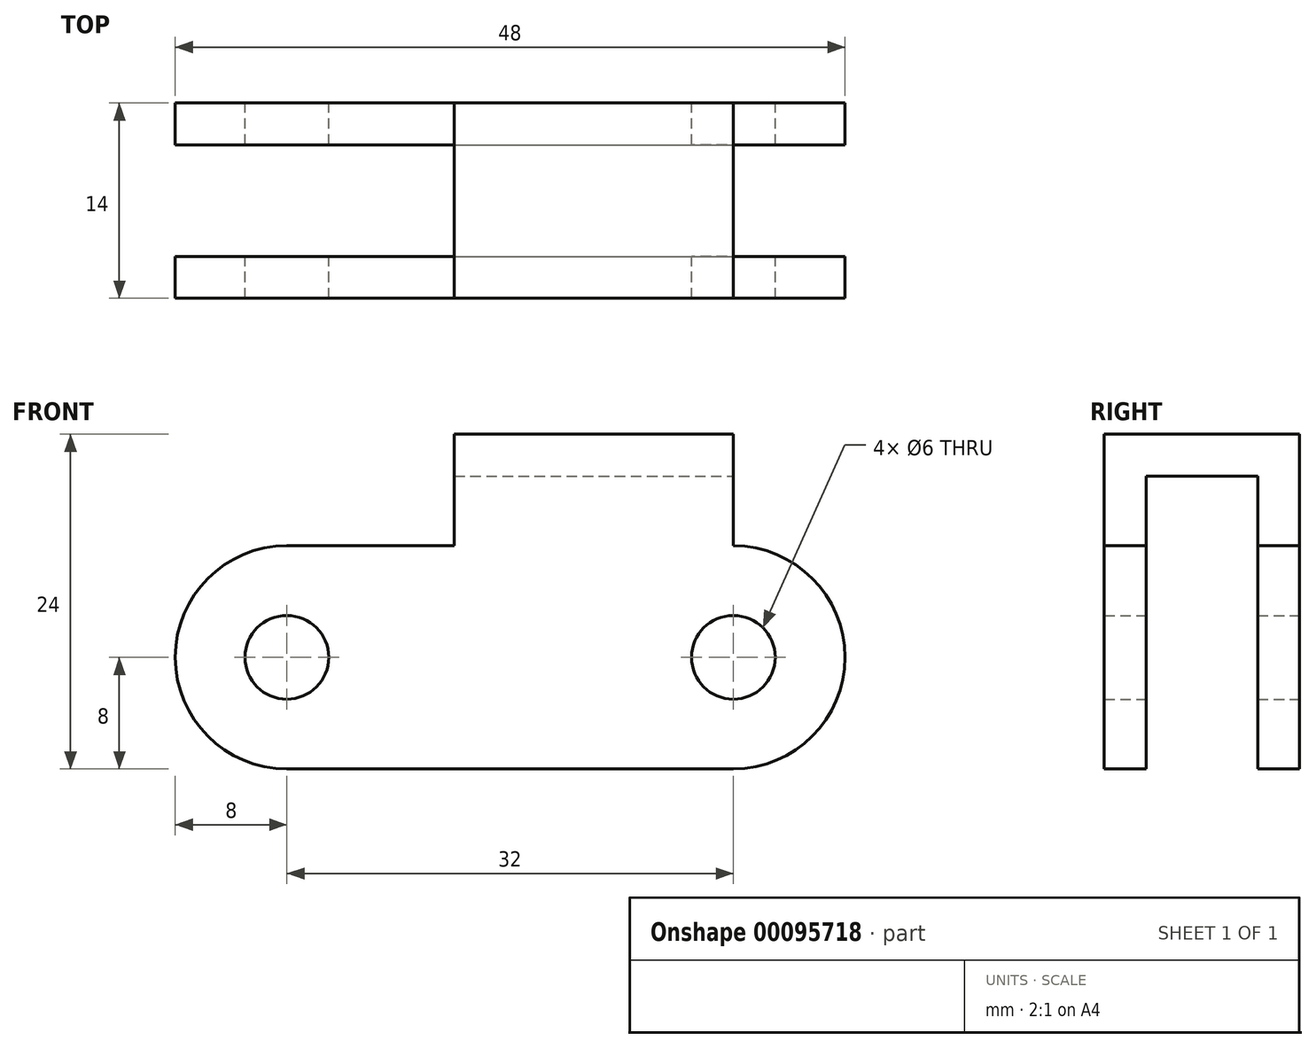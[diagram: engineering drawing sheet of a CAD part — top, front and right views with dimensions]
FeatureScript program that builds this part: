
annotation { "Feature Type Name" : "Feature", "Feature Type Description" : "" }
export const myFeature = defineFeature(function(context is Context, id is Id, definition is map)
    precondition{}
    {
        {
            var Q0;
            Q0=qCreatedBy(makeId("Front.planeOp"),FACE);
            var sketch = newSketch(context, id + "F0", { "sketchPlane" : qUnion([Q0])});
            skArc(sketch, "E0", {"start": v(-32, 8) * mm, "mid": v(-40, 0) * mm, "end": v(-32, -8) * mm});
            skCircle(sketch, "E1", {"center": v(-32, 0) * mm, "radius": 3 * mm});
            skLineSegment(sketch, "E2", {"start": v(-32, 8) * mm, "end": v(-20, 8) * mm});
            skLineSegment(sketch, "E3", {"start": v(-32, -8) * mm, "end": v(0, -8) * mm});
            skLineSegment(sketch, "E4", {"start": v(0, -8) * mm, "end": v(0, 8) * mm, "construction": true});
            skCircle(sketch, "E5", {"center": v(0, 0) * mm, "radius": 3 * mm});
            skArc(sketch, "E6", {"start": v(0, -8) * mm, "mid": v(8, 0) * mm, "end": v(0, 8) * mm});
            skLineSegment(sketch, "E7", {"start": v(0, 8) * mm, "end": v(0, 16) * mm});
            skLineSegment(sketch, "E8", {"start": v(-20, 8) * mm, "end": v(-20, 16) * mm});
            skLineSegment(sketch, "E9", {"start": v(-20, 16) * mm, "end": v(0, 16) * mm});
            skLineSegment(sketch, "E10", {"start": v(-32, 8) * mm, "end": v(-32, -8) * mm, "construction": true});
            skArc(sketch, "E11", {"start": v(-32, -8) * mm, "mid": v(-24, 0) * mm, "end": v(-32, 8) * mm});
            skArc(sketch, "E12", {"start": v(0, 8) * mm, "mid": v(-8, 0) * mm, "end": v(0, -8) * mm});
            skSolve(sketch);
        }
        {
            var Q0;
            Q0 = qSketchRegion(id + "F0", true);
            extrude(context, id + "F1", {"entities" : qUnion([Q0]), "depth" : 14 * mm});
        }
        {
            var Q0;
            Q0=makeQuery(id+"F1.opExtrude","SWEPT_FACE",FACE,{"disambiguationData":[OSD([sQuery(id+"F0.wireOp",EDGE,"E2")])]});
            var Q1;
            Q1=makeQuery(id+"F1.opExtrude","SWEPT_FACE",FACE,{"disambiguationData":[OSD([sQuery(id+"F0.wireOp",EDGE,"E8")])]});
            var Q2;
            Q2=makeQuery(id+"F1.opExtrude","SWEPT_FACE",FACE,{"disambiguationData":[OSD([sQuery(id+"F0.wireOp",EDGE,"E3")])]});
            var Q3;
            Q3=makeQuery(id+"F1.opExtrude","SWEPT_FACE",FACE,{"disambiguationData":[OSD([sQuery(id+"F0.wireOp",EDGE,"E7")])]});
            var Q4;
            Q4=makeQuery(id+"F1.opExtrude","SWEPT_FACE",FACE,{"disambiguationData":[OSD([sQuery(id+"F0.wireOp",EDGE,"E6")])]});
            var Q5;
            Q5=makeQuery(id+"F1.opExtrude","SWEPT_FACE",FACE,{"disambiguationData":[OSD([sQuery(id+"F0.wireOp",EDGE,"E0")])]});
            var Q6;
            Q6=makeQuery(id+"F1.opExtrude","SWEPT_FACE",FACE,{"disambiguationData":[OSD([sQuery(id+"F0.wireOp",EDGE,"E1")])]});
            var Q7;
            Q7=makeQuery(id+"F1.opExtrude","SWEPT_FACE",FACE,{"disambiguationData":[OSD([sQuery(id+"F0.wireOp",EDGE,"E5")])]});
            shell(context, id + "F2", {"entities" : qUnion([Q0, Q1, Q2, Q3, Q4, Q5, Q6, Q7]), "thickness" : 3 * mm});
        }
    });
